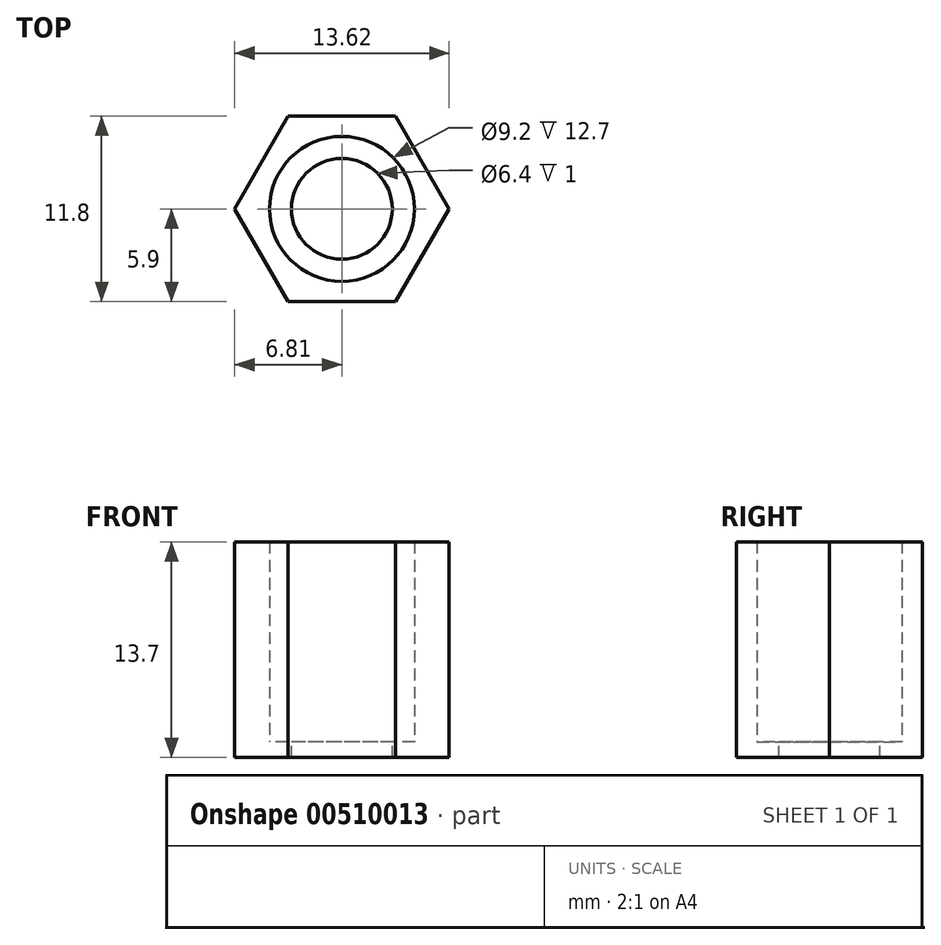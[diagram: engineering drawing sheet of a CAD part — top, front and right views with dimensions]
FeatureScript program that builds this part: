
annotation { "Feature Type Name" : "Feature", "Feature Type Description" : "" }
export const myFeature = defineFeature(function(context is Context, id is Id, definition is map)
    precondition{}
    {
        {
            var Q0;
            Q0=qCreatedBy(makeId("Top.planeOp"),FACE);
            var sketch = newSketch(context, id + "F0", { "sketchPlane" : qUnion([Q0])});
            skCircle(sketch, "E0", {"center": v(0, 0) * mm, "radius": 3.2 * mm});
            skCircle(sketch, "E1.cCircle", {"center": v(0, 0) * mm, "radius": 5.9 * mm, "construction": true});
            skLineSegment(sketch, "E1.0", {"start": v(-3.4, 5.9) * mm, "end": v(3.4, 5.9) * mm});
            skLineSegment(sketch, "E1.1", {"start": v(3.4, 5.9) * mm, "end": v(6.81, 0) * mm});
            skLineSegment(sketch, "E1.2", {"start": v(6.81, 0) * mm, "end": v(3.4, -5.9) * mm});
            skLineSegment(sketch, "E1.3", {"start": v(3.4, -5.9) * mm, "end": v(-3.4, -5.9) * mm});
            skLineSegment(sketch, "E1.4", {"start": v(-3.4, -5.9) * mm, "end": v(-6.81, 0) * mm});
            skLineSegment(sketch, "E1.5", {"start": v(-6.81, 0) * mm, "end": v(-3.4, 5.9) * mm});
            skPoint(sketch, "E1.0.midPoint", {"position": v(0, 5.9) * mm});
            skCircle(sketch, "E2", {"center": v(0, 0) * mm, "radius": 4.6 * mm});
            skSolve(sketch);
        }
        {
            var Q0;
            Q0=makeQuery(id+"F0.imprint","IMPRINT",FACE,{"disambiguationData":[TD([[makeQuery(id+"F0.imprint","IMPRINT",EDGE,{"derivedFrom":sQuery(id+"F0.wireOp",EDGE,"E1.0")}),-1.0]])]});
            extrude(context, id + "F1", {"entities" : qUnion([Q0]), "depth" : 12.7 * mm});
        }
        {
            var Q0;
            Q0=makeQuery(id+"F0.imprint","IMPRINT",FACE,{"disambiguationData":[TD([[makeQuery(id+"F0.imprint","IMPRINT",EDGE,{"derivedFrom":sQuery(id+"F0.wireOp",EDGE,"E0")}),-1.0]])]});
            var Q1;
            Q1=makeQuery(id+"F0.imprint","IMPRINT",FACE,{"disambiguationData":[TD([[makeQuery(id+"F0.imprint","IMPRINT",EDGE,{"derivedFrom":sQuery(id+"F0.wireOp",EDGE,"E1.0")}),-1.0]])]});
            extrude(context, id + "F2", {"entities" : qUnion([Q0, Q1]), "operationType" : NewBodyOperationType.ADD, "oppositeDirection" : true, "depth" : 1 * mm});
        }
    });
